# Revit family: Lighting-Adjustable-Lucifer-Micro-Cylinder
name_source: partatom
category: Lighting Fixtures
revit_build: Autodesk Revit 2015 (Build: 20140606_1530(x64)
units: mm (PartAtom-declared; Revit-internal decimal feet)

## types (3) — shared parameters
Apparent Load = 0 VA
Color Filter = 16777215
Default Elevation = 2"
Description = Micro-Cylinder Luminare
Dimming Lamp Color Temperature Shift = <None>
Emergency Fixture = Yes
Emit Shape Visible in Rendering = No
Finish = Metal - Finish
Manufacturer = Lucifer Lighting
Number of Poles = 1
Photometric Web File = generic
Power Factor = 1
Tilt Angle = 90.00°
URL = http://luciferlighting.com
Voltage = 120 V

## per-type parameters (varying)
| type | Emit from Circle Diameter | Fixture Radius | Length |
| CY1-AD | 2 1/2" | 1 1/4" | 3 51/64" |
| CY2-AD | 3 1/8" | 1 9/16" | 4 29/32" |
| CY3-AD | 3 1/4" | 1 5/8" | 5 13/64" |

note: column(s) folded — value = type name in every type: Model

## geometry (parser evidence)
native form markers: Sweep x3
no freeform markers — native parametric forms only
